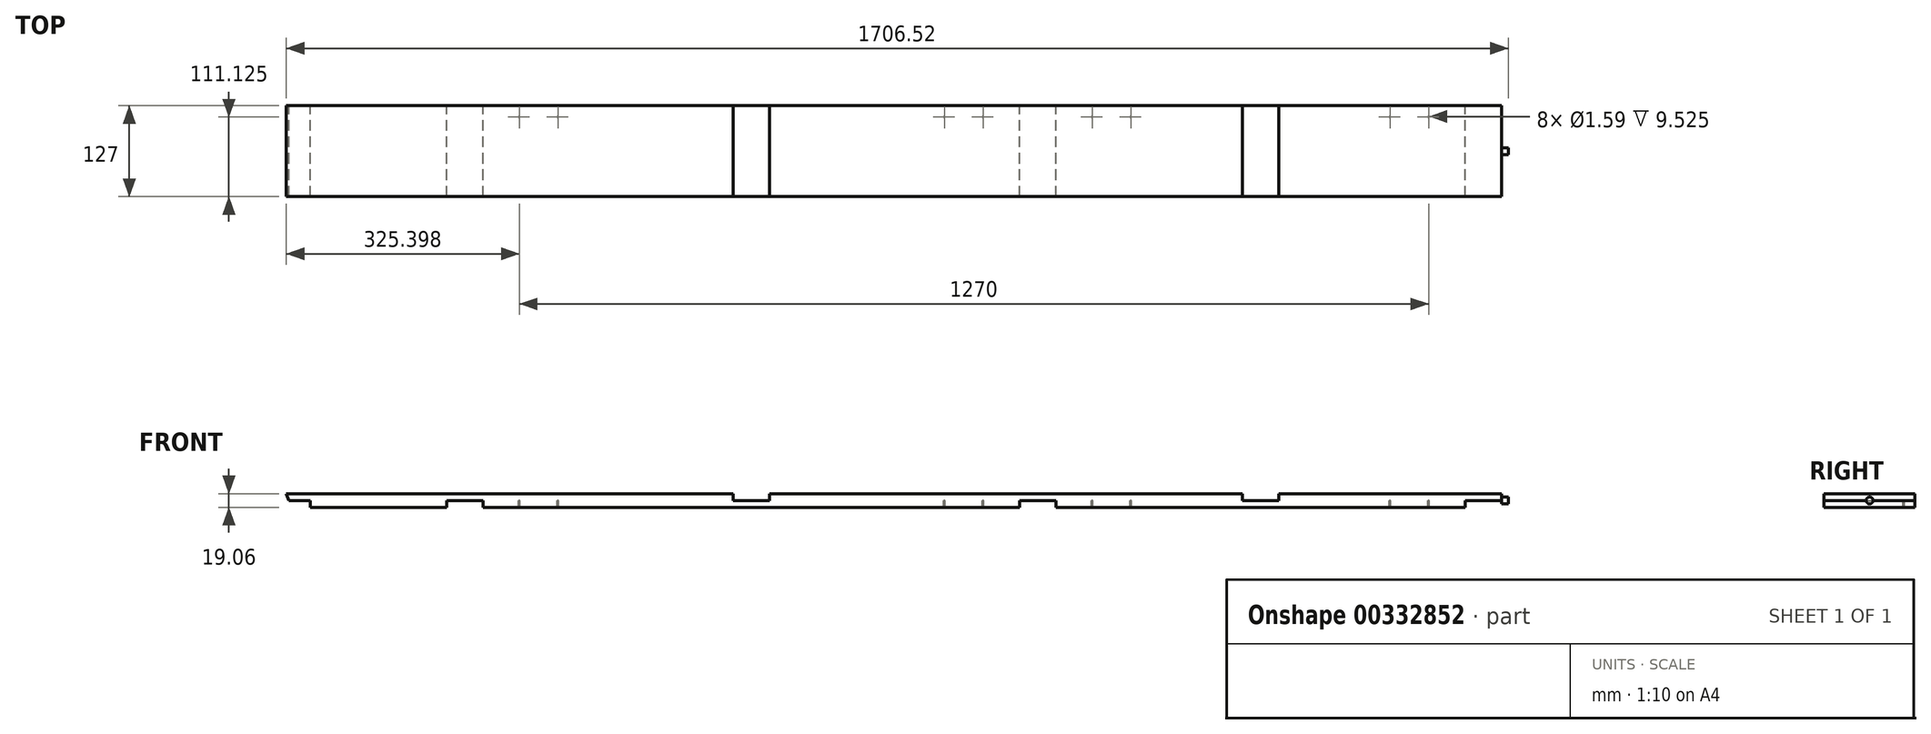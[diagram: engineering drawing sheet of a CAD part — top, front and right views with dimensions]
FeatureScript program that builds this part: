
annotation { "Feature Type Name" : "Feature", "Feature Type Description" : "" }
export const myFeature = defineFeature(function(context is Context, id is Id, definition is map)
    precondition{}
    {
        {
            var Q0;
            Q0=qCreatedBy(makeId("Front.planeOp"),FACE);
            var sketch = newSketch(context, id + "F0", { "sketchPlane" : qUnion([Q0])});
            skLineSegment(sketch, "E0.bottom", {"start": v(9.6, -9.52) * mm, "end": v(200.1, -9.52) * mm});
            skLineSegment(sketch, "E0.right", {"start": v(1673.3, 0) * mm, "end": v(1673.3, 9.52) * mm});
            skLineSegment(sketch, "E1", {"start": v(-19.76, 0) * mm, "end": v(-23.7, 9.52) * mm});
            skLineSegment(sketch, "E2.top", {"start": v(200.1, 0) * mm, "end": v(250.9, 0) * mm});
            skLineSegment(sketch, "E2.left", {"start": v(200.1, -9.52) * mm, "end": v(200.1, 0) * mm});
            skLineSegment(sketch, "E2.right", {"start": v(250.9, -9.52) * mm, "end": v(250.9, 0) * mm});
            skLineSegment(sketch, "E3.trimOffspring", {"start": v(250.9, -9.52) * mm, "end": v(1000.2, -9.52) * mm});
            skLineSegment(sketch, "E4.top", {"start": v(1000.2, 0) * mm, "end": v(1051, 0) * mm});
            skLineSegment(sketch, "E4.left", {"start": v(1000.2, -9.52) * mm, "end": v(1000.2, 0) * mm});
            skLineSegment(sketch, "E4.right", {"start": v(1051, -9.52) * mm, "end": v(1051, 0) * mm});
            skLineSegment(sketch, "E5.trimOffspring", {"start": v(1051, -9.52) * mm, "end": v(1622.5, -9.52) * mm});
            skLineSegment(sketch, "E6.top", {"start": v(1622.5, 0) * mm, "end": v(1673.3, 0) * mm});
            skLineSegment(sketch, "E6.left", {"start": v(1622.5, -9.52) * mm, "end": v(1622.5, 0) * mm});
            skPoint(sketch, "E7.orphan", {"position": v(1673.3, -9.52) * mm});
            skLineSegment(sketch, "E8", {"start": v(1673.3, 9.53) * mm, "end": v(1362.15, 9.53) * mm});
            skLineSegment(sketch, "E9", {"start": v(625.55, -9.53) * mm, "end": v(625.55, 19.05) * mm, "construction": true});
            skLineSegment(sketch, "E10", {"start": v(1336.75, -9.52) * mm, "end": v(1336.75, 9.53) * mm, "construction": true});
            skLineSegment(sketch, "E11.top", {"start": v(650.95, 0) * mm, "end": v(600.15, 0) * mm});
            skLineSegment(sketch, "E11.left", {"start": v(650.95, 9.53) * mm, "end": v(650.95, 0) * mm});
            skLineSegment(sketch, "E11.right", {"start": v(600.15, 9.53) * mm, "end": v(600.15, 0) * mm});
            skPoint(sketch, "E11.middle", {"position": v(625.55, 9.53) * mm});
            skPoint(sketch, "E11.middle.positionSnap0", {"position": v(625.55, 19.05) * mm});
            skPoint(sketch, "E11.cornerSnap0", {"position": v(625.55, 19.05) * mm});
            skPoint(sketch, "E11.centerSnap0", {"position": v(625.55, 19.05) * mm});
            skLineSegment(sketch, "E12.top", {"start": v(1311.35, 0) * mm, "end": v(1362.15, 0) * mm});
            skLineSegment(sketch, "E12.left", {"start": v(1311.35, 9.53) * mm, "end": v(1311.35, 0) * mm});
            skLineSegment(sketch, "E12.right", {"start": v(1362.15, 9.53) * mm, "end": v(1362.15, 0) * mm});
            skPoint(sketch, "E12.middle", {"position": v(1336.75, 9.53) * mm});
            skPoint(sketch, "E12.middle.positionSnap0", {"position": v(1336.75, 51.1) * mm});
            skPoint(sketch, "E12.centerSnap0", {"position": v(1336.75, 51.1) * mm});
            skPoint(sketch, "E13.orphan", {"position": v(1362.15, 19.05) * mm});
            skLineSegment(sketch, "E14.trimOffspring", {"start": v(1311.35, 9.53) * mm, "end": v(625.55, 9.53) * mm});
            skPoint(sketch, "E15.orphan", {"position": v(1311.35, 19.05) * mm});
            skLineSegment(sketch, "E16.trimOffspring", {"start": v(600.15, 9.53) * mm, "end": v(-23.7, 9.52) * mm});
            skPoint(sketch, "E17.orphan", {"position": v(650.95, 19.05) * mm});
            skPoint(sketch, "E18.orphan", {"position": v(600.15, 19.05) * mm});
            skPoint(sketch, "E19.orphan", {"position": v(625.55, 47.62) * mm});
            skLineSegment(sketch, "E20.trimOffspring", {"start": v(1336.75, 51.1) * mm, "end": v(1336.75, 111.7) * mm, "construction": true});
            skLineSegment(sketch, "E21", {"start": v(-19.76, 0) * mm, "end": v(9.6, 0) * mm});
            skLineSegment(sketch, "E22", {"start": v(9.6, -9.52) * mm, "end": v(9.6, 0) * mm});
            skPoint(sketch, "E23.top.start.orphan", {"position": v(0, -47.7) * mm});
            skSolve(sketch);
        }
        {
            var Q0;
            Q0=makeQuery(id+"F0.imprint","IMPRINT",FACE,{"disambiguationData":[TD([[makeQuery(id+"F0.imprint","IMPRINT",EDGE,{"derivedFrom":sQuery(id+"F0.wireOp",EDGE,"E0.bottom")}),1.0]])]});
            extrude(context, id + "F1", {"entities" : qUnion([Q0]), "endBound" : BoundingType.SYMMETRIC, "depth" : 127 * mm});
        }
        {
            var Q0;
            Q0=qCreatedBy(makeId("Right.planeOp"),FACE);
            cPlane(context, id + "F2", {"entities" : qUnion([Q0]), "cplaneType" : CPlaneType.OFFSET, "offset" : 1673.3 * mm, "width" : 152.4 * mm, "height" : 152.4 * mm});
        }
        {
            var Q0;
            Q0=qCreatedBy(id+"F2.planeOp",FACE);
            var sketch = newSketch(context, id + "F3", { "sketchPlane" : qUnion([Q0])});
            skCircle(sketch, "E24", {"center": v(0, 0) * mm, "radius": 4.76 * mm});
            skSolve(sketch);
        }
        {
            var Q0;
            Q0=qSketchRegion(id+"F3",true);
            extrude(context, id + "F4", {"entities" : qUnion([Q0]), "operationType" : NewBodyOperationType.ADD, "depth" : 9.52 * mm});
        }
        {
            var Q0;
            Q0=qCreatedBy(makeId("Top.planeOp"),FACE);
            var sketch = newSketch(context, id + "F5", { "sketchPlane" : qUnion([Q0])});
            skCircle(sketch, "E25", {"center": v(301.7, 47.62) * mm, "radius": 0.8 * mm});
            skCircle(sketch, "E26", {"center": v(355.67, 47.62) * mm, "radius": 0.8 * mm});
            skCircle(sketch, "E27", {"center": v(895.42, 47.62) * mm, "radius": 0.8 * mm});
            skCircle(sketch, "E28", {"center": v(949.4, 47.62) * mm, "radius": 0.8 * mm});
            skCircle(sketch, "E29", {"center": v(1101.8, 47.62) * mm, "radius": 0.8 * mm});
            skCircle(sketch, "E30", {"center": v(1155.77, 47.62) * mm, "radius": 0.8 * mm});
            skCircle(sketch, "E31", {"center": v(1517.72, 47.63) * mm, "radius": 0.8 * mm});
            skCircle(sketch, "E32", {"center": v(1571.7, 47.63) * mm, "radius": 0.8 * mm});
            skSolve(sketch);
        }
        {
            var Q0;
            Q0 = qSketchRegion(id + "F5", true);
            extrude(context, id + "F6", {"entities" : qUnion([Q0]), "operationType" : NewBodyOperationType.REMOVE, "oppositeDirection" : true, "depth" : 12.7 * mm});
        }
        {
            var Q0;
            Q0=qCreatedBy(makeId("Top.planeOp"),FACE);
            var sketch = newSketch(context, id + "F7", { "sketchPlane" : qUnion([Q0])});
            skLineSegment(sketch, "E33", {"start": v(625.55, 420.6) * mm, "end": v(625.55, -625.3) * mm, "construction": true});
            skLineSegment(sketch, "E34.bottom", {"start": v(650.95, 115.96) * mm, "end": v(600.15, 115.96) * mm});
            skLineSegment(sketch, "E34.top", {"start": v(650.95, -115.96) * mm, "end": v(600.15, -115.96) * mm});
            skLineSegment(sketch, "E34.left", {"start": v(650.95, 115.96) * mm, "end": v(650.95, -115.96) * mm});
            skLineSegment(sketch, "E34.right", {"start": v(600.15, 115.96) * mm, "end": v(600.15, -115.96) * mm});
            skPoint(sketch, "E34.middle", {"position": v(625.55, 0) * mm});
            skSolve(sketch);
        }
        {
            var Q0;
            Q0 = qSketchRegion(id + "F7", true);
            extrude(context, id + "F8", {"entities" : qUnion([Q0]), "operationType" : NewBodyOperationType.REMOVE, "depth" : 25.4 * mm});
        }
    });
